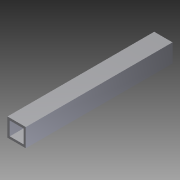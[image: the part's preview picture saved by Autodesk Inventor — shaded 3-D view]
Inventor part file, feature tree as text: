
AUTODESK INVENTOR PART (.ipt)
format: ipt  version: 2012 (Build 160160000, 160)  size: 75,264 bytes
history: native  units: in
note: dims shown in document units (in); Inventor stores cm internally (conversion verified against a paired STEP export)
features: extrude x1, shell x1, sketch x1
ambient origin geometry x8: Origin, YZ Plane, XZ Plane, XY Plane, X Axis, Y Axis, Z Axis, Center Point
bodies: Solid1 (feature_tree)
feature tree (3):
  extrude  "Extrusion1"  Depth=1.0in
  shell  "Shell1"  Thickness=8.0in
  sketch  "Sketch1"  dims[d0=1.0in d1=1.0in d2=8.0in d3=0.0in d4=0.125in]
